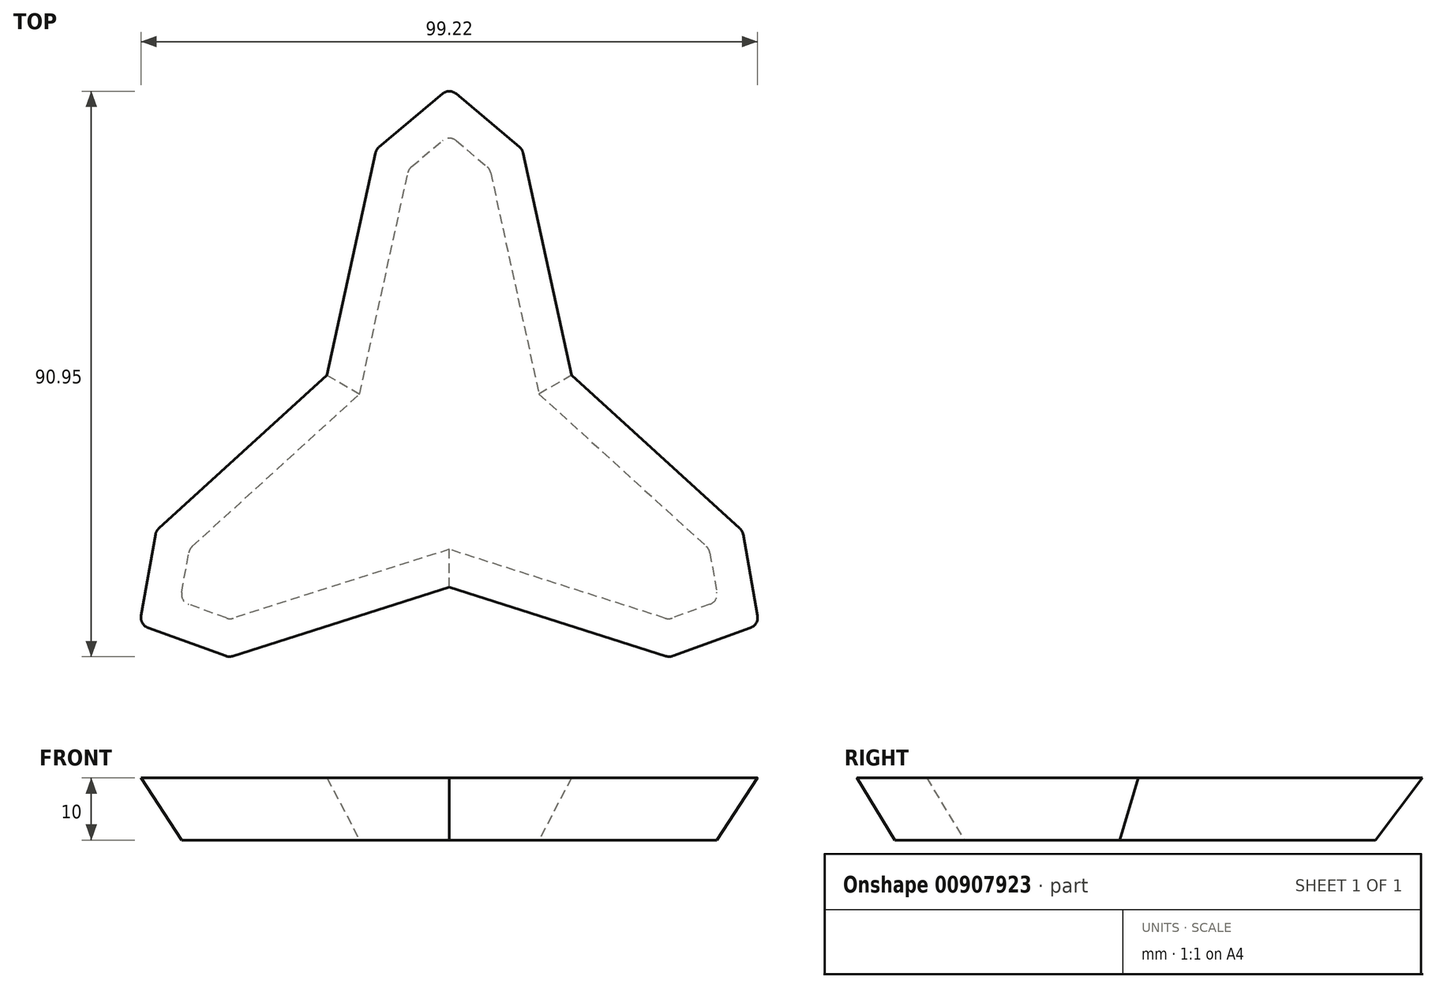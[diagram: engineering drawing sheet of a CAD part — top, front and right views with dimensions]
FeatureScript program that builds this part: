
annotation { "Feature Type Name" : "Feature", "Feature Type Description" : "" }
export const myFeature = defineFeature(function(context is Context, id is Id, definition is map)
    precondition{}
    {
        {
            var Q0;
            Q0=qCreatedBy(makeId("Top.planeOp"),FACE);
            var sketch = newSketch(context, id + "F0", { "sketchPlane" : qUnion([Q0])});
            skCircle(sketch, "E0", {"center": v(0, 0) * mm, "radius": 50 * mm, "construction": true});
            skLineSegment(sketch, "E1", {"start": v(0, 0) * mm, "end": v(-43.3, -25) * mm, "construction": true});
            skLineSegment(sketch, "E2", {"start": v(0, 0) * mm, "end": v(0, 50) * mm, "construction": true});
            skLineSegment(sketch, "E3", {"start": v(0, 0) * mm, "end": v(43.3, -25) * mm, "construction": true});
            skLineSegment(sketch, "E4", {"start": v(0, 50) * mm, "end": v(-6.53, 44.52) * mm});
            skCircle(sketch, "E5", {"center": v(0, 0) * mm, "radius": 10 * mm});
            skLineSegment(sketch, "E6", {"start": v(0, 0) * mm, "end": v(-52.94, 30.56) * mm, "construction": true});
            skLineSegment(sketch, "E7", {"start": v(0, 0) * mm, "end": v(0, -34.14) * mm, "construction": true});
            skLineSegment(sketch, "E8", {"start": v(0, 0) * mm, "end": v(50.12, 28.94) * mm, "construction": true});
            skLineSegment(sketch, "E9", {"start": v(-6.53, 44.52) * mm, "end": v(-14.43, 8.33) * mm});
            skLineSegment(sketch, "E10", {"start": v(-14.43, 8.33) * mm, "end": v(-41.82, -16.61) * mm});
            skLineSegment(sketch, "E11", {"start": v(-41.82, -16.61) * mm, "end": v(-43.3, -25) * mm});
            skLineSegment(sketch, "E12", {"start": v(-43.3, -25) * mm, "end": v(-35.3, -27.91) * mm});
            skLineSegment(sketch, "E13", {"start": v(-35.3, -27.91) * mm, "end": v(0, -16.67) * mm});
            skLineSegment(sketch, "E14", {"start": v(0, -16.67) * mm, "end": v(35.3, -27.91) * mm});
            skLineSegment(sketch, "E15", {"start": v(35.3, -27.91) * mm, "end": v(43.3, -25) * mm});
            skLineSegment(sketch, "E16", {"start": v(14.43, 8.33) * mm, "end": v(6.53, 44.52) * mm});
            skLineSegment(sketch, "E17", {"start": v(0, 50) * mm, "end": v(6.53, 44.52) * mm});
            skCircle(sketch, "E18", {"center": v(0, 0) * mm, "radius": 45 * mm, "construction": true});
            skLineSegment(sketch, "E19", {"start": v(43.3, -25) * mm, "end": v(41.82, -16.61) * mm});
            skLineSegment(sketch, "E20", {"start": v(41.82, -16.61) * mm, "end": v(14.43, 8.33) * mm});
            skSolve(sketch);
        }
        {
            var Q0;
            Q0=makeQuery(id+"F0.imprint","IMPRINT",FACE,{"disambiguationData":[TD([[makeQuery(id+"F0.imprint","IMPRINT",EDGE,{"derivedFrom":sQuery(id+"F0.wireOp",EDGE,"E4")}),1.0]])]});
            var Q1;
            Q1=makeQuery(id+"F0.imprint","IMPRINT",FACE,{"disambiguationData":[TD([[makeQuery(id+"F0.imprint","IMPRINT",EDGE,{"derivedFrom":sQuery(id+"F0.wireOp",EDGE,"E5")}),1.0]])]});
            extrude(context, id + "F1", {"entities" : qUnion([Q0, Q1]), "depth" : 10 * mm, "offsetDistance" : 25 * mm, "hasDraft" : true, "draftAngle" : 30 * degree});
        }
        {
            var Q0;
            Q0=makeQuery(id+"F1.opExtrude","SWEPT_EDGE",EDGE,{"disambiguationData":[OSD([sQuery(id+"F0.wireOp",EDGE,"E4"),sQuery(id+"F0.wireOp",EDGE,"E17")])]});
            var Q1;
            Q1=makeQuery(id+"F1.opExtrude","SWEPT_EDGE",EDGE,{"disambiguationData":[OSD([sQuery(id+"F0.wireOp",EDGE,"E16"),sQuery(id+"F0.wireOp",EDGE,"E17")])]});
            var Q2;
            Q2=makeQuery(id+"F1.opExtrude","SWEPT_EDGE",EDGE,{"disambiguationData":[OSD([sQuery(id+"F0.wireOp",EDGE,"E4"),sQuery(id+"F0.wireOp",EDGE,"E9")])]});
            var Q3;
            Q3=makeQuery(id+"F1.opExtrude","SWEPT_EDGE",EDGE,{"disambiguationData":[OSD([sQuery(id+"F0.wireOp",EDGE,"E19"),sQuery(id+"F0.wireOp",EDGE,"E20")])]});
            var Q4;
            Q4=makeQuery(id+"F1.opExtrude","SWEPT_EDGE",EDGE,{"disambiguationData":[OSD([sQuery(id+"F0.wireOp",EDGE,"E15"),sQuery(id+"F0.wireOp",EDGE,"E19")])]});
            var Q5;
            Q5=makeQuery(id+"F1.opExtrude","SWEPT_EDGE",EDGE,{"disambiguationData":[OSD([sQuery(id+"F0.wireOp",EDGE,"E14"),sQuery(id+"F0.wireOp",EDGE,"E15")])]});
            var Q6;
            Q6=makeQuery(id+"F1.opExtrude","SWEPT_EDGE",EDGE,{"disambiguationData":[OSD([sQuery(id+"F0.wireOp",EDGE,"E10"),sQuery(id+"F0.wireOp",EDGE,"E11")])]});
            var Q7;
            Q7=makeQuery(id+"F1.opExtrude","SWEPT_EDGE",EDGE,{"disambiguationData":[OSD([sQuery(id+"F0.wireOp",EDGE,"E11"),sQuery(id+"F0.wireOp",EDGE,"E12")])]});
            var Q8;
            Q8=makeQuery(id+"F1.opExtrude","SWEPT_EDGE",EDGE,{"disambiguationData":[OSD([sQuery(id+"F0.wireOp",EDGE,"E12"),sQuery(id+"F0.wireOp",EDGE,"E13")])]});
            fillet(context, id + "F2", {"entities" : qUnion([Q0, Q1, Q2, Q3, Q4, Q5, Q6, Q7, Q8]), "radius" : 2 * mm, "tangentPropagation" : true, "allowEdgeOverflow" : false});
        }
    });
